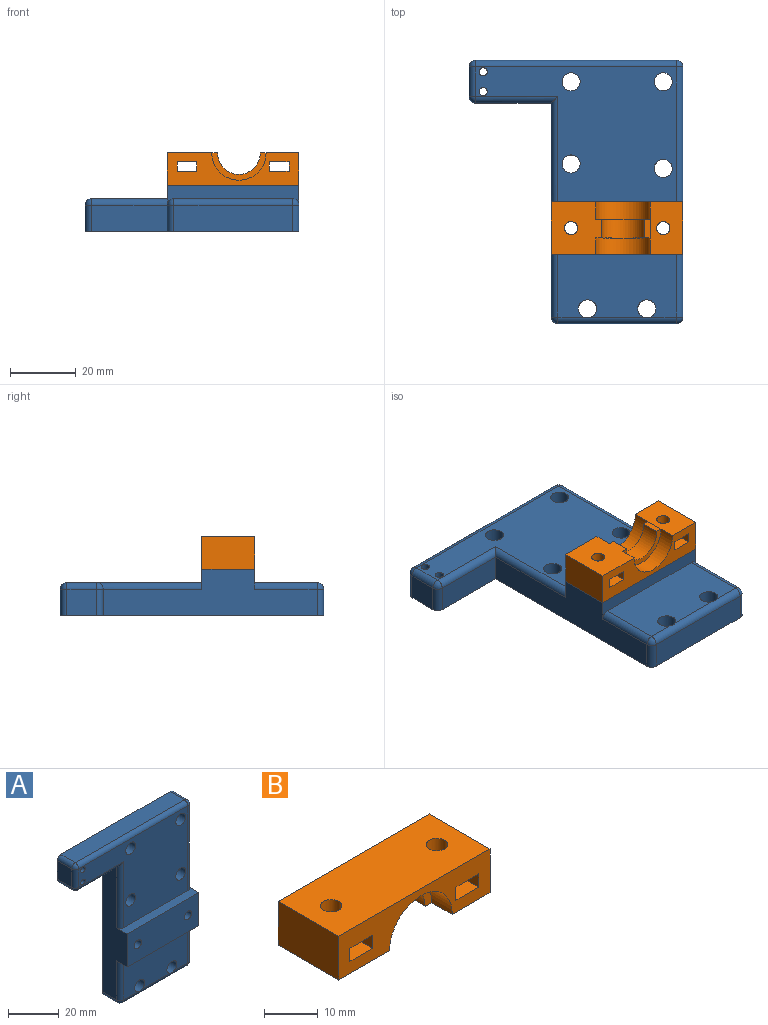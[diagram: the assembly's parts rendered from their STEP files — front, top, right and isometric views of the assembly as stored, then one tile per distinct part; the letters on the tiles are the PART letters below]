
ASSEMBLY  parts=2 mates=1
PART A: 44 faces, bbox 65x14x80 mm
  f0: plane 61x41mm, normal (0,-1,0), area 1596.1mm2, adj f6,f9,f10,f11,f12,f14,f17,f33
  f1: plane 76x14mm, normal (1,0,0), area 704mm2, adj f16,f17,f18,f21,f26,f27,f40,f43
  f2: plane 61x8mm, normal (0,0,1), area 488mm2, adj f16,f38,f41,f43
  f3: plane 9x8mm, normal (-1,0,0), area 72mm2, adj f16,f35,f37,f38
  f4: plane 23x8mm, normal (0,0,-1), area 184mm2, adj f5,f16,f34,f35
  f5: plane 65x14mm, normal (-1,0,0), area 616mm2, adj f4,f16,f17,f18,f21,f30,f32,f33
  f6: cylinder r=1.25mm len=10mm, axis (0,1,0), area 78.5mm2, adj f0,f16
  f7: cylinder r=2.75mm len=10mm, axis (0,1,0), area 172.8mm2, adj f15,f16,f29
  f8: cylinder r=2.75mm len=10mm, axis (0,1,0), area 172.8mm2, adj f15,f16,f29
  f9: cylinder r=2.75mm len=10mm, axis (0,1,0), area 172.8mm2, adj f0,f16
  f10: cylinder r=2.75mm len=10mm, axis (0,1,0), area 172.8mm2, adj f0,f16
  f11: cylinder r=2.75mm len=10mm, axis (0,1,0), area 172.8mm2, adj f0,f16
  f12: cylinder r=2.75mm len=10mm, axis (0,1,0), area 172.8mm2, adj f0,f16
  f13: plane 36x8mm, normal (0,0,-1), area 288mm2, adj f16,f27,f29,f30
  f14: cylinder r=1.25mm len=10mm, axis (0,1,0), area 78.5mm2, adj f0,f16
  f15: plane 36x19mm, normal (0,-1,0), area 637.3mm2, adj f7,f8,f18,f26,f29,f32
  f16: plane 80x65mm, normal (0,1,0), area 3318.1mm2, adj f1,f2,f3,f4,f5,f6,f7,f8
  f17: plane 40x6mm, normal (0,0,1), area 161.7mm2, adj f0,f1,f5,f21,f33,f40
  f18: plane 40x6mm, normal (0,0,-1), area 161.7mm2, adj f1,f5,f15,f21,f26,f32
  f19: cylinder r=2mm len=14mm, axis (0,1,0), area 175.9mm2, adj f16,f21
  f20: cylinder r=2mm len=14mm, axis (0,1,0), area 175.9mm2, adj f16,f21
  f21: plane 40x16mm, normal (0,-1,0), area 614.9mm2, adj f1,f5,f17,f18,f19,f20
  f22: cylinder r=2mm len=9mm, axis (0,1,0), area 113.1mm2, adj f16,f23
  f23: plane 4x4mm, normal (0,1,0), area 12.6mm2, adj f22
  f24: cylinder r=2mm len=9mm, axis (0,1,0), area 113.1mm2, adj f16,f25
  f25: plane 4x4mm, normal (0,1,0), area 12.6mm2, adj f24
  f26: cylinder r=2mm len=19mm, axis (0,0,-1), area 59.7mm2, adj f1,f15,f18,f28
  f27: cylinder r=2mm len=8mm, axis (0,-1,0), area 25.1mm2, adj f1,f13,f16,f28
  f28: sphere r=2mm, area 6.3mm2, adj f26,f27,f29
  f29: cylinder r=2mm len=36mm, axis (-1,0,0), area 112.3mm2, adj f7,f8,f13,f15,f28,f31
  f30: cylinder r=2mm len=8mm, axis (0,1,0), area 25.1mm2, adj f5,f13,f16,f31
  f31: sphere r=2mm, area 6.3mm2, adj f29,f30,f32
  f32: cylinder r=2mm len=19mm, axis (0,0,1), area 59.7mm2, adj f5,f15,f18,f31
  f33: cylinder r=2mm len=32mm, axis (0,0,1), area 96.5mm2, adj f0,f5,f17,f34
  f34: cylinder r=2mm len=25mm, axis (-1,0,0), area 74.5mm2, adj f0,f4,f33,f36
  f35: cylinder r=2mm len=8mm, axis (0,1,0), area 25.1mm2, adj f3,f4,f16,f36
  f36: sphere r=2mm, area 6.3mm2, adj f34,f35,f37
  f37: cylinder r=2mm len=9mm, axis (0,0,1), area 28.3mm2, adj f0,f3,f36,f39
  f38: cylinder r=2mm len=8mm, axis (0,-1,0), area 25.1mm2, adj f2,f3,f16,f39
  f39: sphere r=2mm, area 6.3mm2, adj f37,f38,f41
  f40: cylinder r=2mm len=41mm, axis (0,0,-1), area 128.8mm2, adj f0,f1,f17,f42
  f41: cylinder r=2mm len=61mm, axis (1,0,0), area 191.6mm2, adj f0,f2,f39,f42
  f42: sphere r=2mm, area 6.3mm2, adj f40,f41,f43
  f43: cylinder r=2mm len=8mm, axis (0,1,0), area 25.1mm2, adj f1,f2,f16,f42
PART B: 25 faces, bbox 40x16x10 mm
  f0: plane 40x10mm, normal (0,-1,0), area 254.4mm2, adj f4,f6,f7,f8,f9,f10,f17,f18
  f1: plane 40x10mm, normal (0,1,0), area 254.4mm2, adj f5,f6,f7,f8,f9,f10,f17,f18
  f2: cylinder r=2mm len=4.23mm, axis (0,0,1), area 53.2mm2, adj f8,f21
  f3: cylinder r=2mm len=4.23mm, axis (0,0,1), area 53.2mm2, adj f8,f17
  f4: cylinder r=8.25mm len=16.5mm, axis (0,1,0), area 141.7mm2, adj f0,f6,f10,f13
  f5: cylinder r=8.25mm len=16.5mm, axis (0,1,0), area 131.2mm2, adj f1,f6,f10,f12
  f6: plane 16x10mm, normal (0,0,-1), area 147.4mm2, adj f0,f1,f4,f5,f7,f11,f16
  f7: plane 16x10mm, normal (1,0,0), area 160mm2, adj f0,f1,f6,f8
  f8: plane 40x16mm, normal (0,0,1), area 614.9mm2, adj f0,f1,f2,f3,f7,f9
  f9: plane 16x10mm, normal (-1,0,0), area 160mm2, adj f0,f1,f8,f10
  f10: plane 16x15.25mm, normal (0,0,-1), area 213.2mm2, adj f0,f1,f4,f5,f9,f12,f13,f14
  f11: plane 5.6x1.75mm, normal (-0.04,0,-1), area 9.8mm2, adj f6,f12,f13,f14
  f12: plane 16.5x8.41mm, normal (0,1,0), area 41.1mm2, adj f5,f10,f11,f14
  f13: plane 16.5x8.41mm, normal (0,-1,0), area 41.1mm2, adj f4,f10,f11,f14
  f14: cylinder r=6.5mm len=13mm, axis (0,1,0), area 115.8mm2, adj f10,f11,f12,f13
  f15: cylinder r=2mm len=4mm, axis (0,0,1), area 34.8mm2, adj f10,f22
  f16: cylinder r=2mm len=4mm, axis (0,0,1), area 34.8mm2, adj f6,f18
  f17: plane 16x6mm, normal (0,0,-1), area 83.4mm2, adj f0,f1,f3,f19,f20
  f18: plane 16x6mm, normal (0,0,1), area 83.4mm2, adj f0,f1,f16,f19,f20
  f19: plane 16x3mm, normal (-1,0,0), area 48mm2, adj f0,f1,f17,f18
  f20: plane 16x3mm, normal (1,0,0), area 48mm2, adj f0,f1,f17,f18
  f21: plane 16x6mm, normal (0,0,-1), area 83.4mm2, adj f0,f1,f2,f23,f24
  f22: plane 16x6mm, normal (0,0,1), area 83.4mm2, adj f0,f1,f15,f23,f24
  f23: plane 16x3mm, normal (-1,0,0), area 48mm2, adj f0,f1,f21,f22
  f24: plane 16x3mm, normal (1,0,0), area 48mm2, adj f0,f1,f21,f22
PLACE A rot(axis=(-1,0,0),90deg) t=(1.46,16.14,-14.99)mm
PLACE B rot(axis=(-1,0,0),180deg) t=(1.46,-42.86,-0.99)mm
MATE fastened B.f8 <-> A.f21  axis (0,0,-1) through (21.46,-34.86,-0.99)mm
